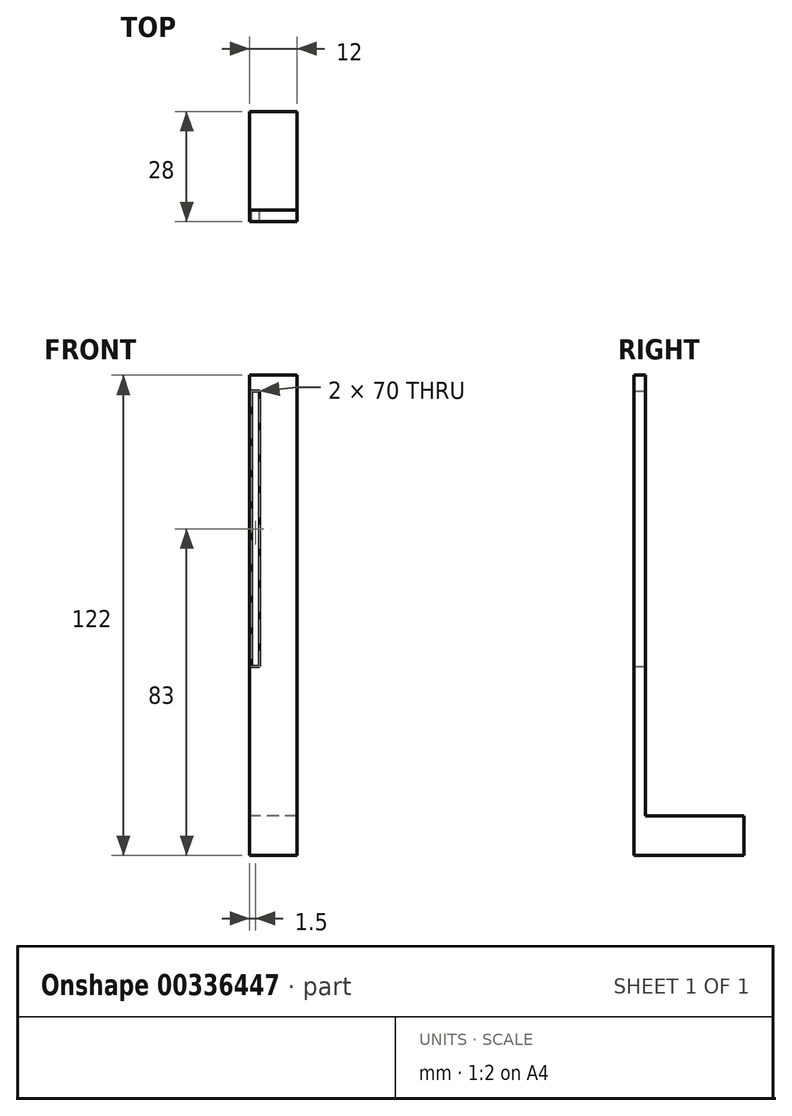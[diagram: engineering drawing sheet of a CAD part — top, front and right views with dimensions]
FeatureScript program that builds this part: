
annotation { "Feature Type Name" : "Feature", "Feature Type Description" : "" }
export const myFeature = defineFeature(function(context is Context, id is Id, definition is map)
    precondition{}
    {
        {
            var Q0;
            Q0=qCreatedBy(makeId("Right.planeOp"),FACE);
            var sketch = newSketch(context, id + "F0", { "sketchPlane" : qUnion([Q0])});
            skLineSegment(sketch, "E0.bottom", {"start": v(0, 0) * mm, "end": v(-3, 0) * mm});
            skLineSegment(sketch, "E0.top", {"start": v(0, 122) * mm, "end": v(-3, 122) * mm});
            skLineSegment(sketch, "E0.left", {"start": v(0, 0) * mm, "end": v(0, 122) * mm});
            skLineSegment(sketch, "E0.right", {"start": v(-3, 0) * mm, "end": v(-3, 122) * mm});
            skSolve(sketch);
        }
        {
            var Q0;
            Q0=qSketchRegion(id+"F0",true);
            extrude(context, id + "F1", {"entities" : qUnion([Q0]), "depth" : 12 * mm});
        }
        {
            var Q0;
            Q0=makeQuery(id+"F1.opExtrude","SWEPT_FACE",FACE,{"disambiguationData":[OSD([sQuery(id+"F0.wireOp",EDGE,"E0.left")])]});
            var sketch = newSketch(context, id + "F2", { "sketchPlane" : qUnion([Q0])});
            skLineSegment(sketch, "E1.bottom", {"start": v(-12, 0) * mm, "end": v(0, 0) * mm});
            skLineSegment(sketch, "E1.top", {"start": v(-12, 10) * mm, "end": v(0, 10) * mm});
            skLineSegment(sketch, "E1.left", {"start": v(-12, 0) * mm, "end": v(-12, 10) * mm});
            skLineSegment(sketch, "E1.right", {"start": v(0, 0) * mm, "end": v(0, 10) * mm});
            skSolve(sketch);
        }
        {
            var Q0;
            Q0=qSketchRegion(id+"F2",true);
            extrude(context, id + "F3", {"entities" : qUnion([Q0]), "operationType" : NewBodyOperationType.ADD, "depth" : 25 * mm});
        }
        {
            var Q0;
            Q0=makeQuery(id+"F1.opExtrude","SWEPT_FACE",FACE,{"disambiguationData":[OSD([sQuery(id+"F0.wireOp",EDGE,"E0.left")])]});
            var sketch = newSketch(context, id + "F4", { "sketchPlane" : qUnion([Q0])});
            skPoint(sketch, "E2.centerSnap0", {"position": v(-1.5, 122) * mm});
            skLineSegment(sketch, "E3", {"start": v(-1.5, 118) * mm, "end": v(-1.5, 48) * mm, "construction": true});
            skLineSegment(sketch, "E4", {"start": v(-1.5, 118) * mm, "end": v(-0.5, 118) * mm});
            skLineSegment(sketch, "E5", {"start": v(-0.5, 118) * mm, "end": v(-0.5, 48) * mm});
            skLineSegment(sketch, "E6", {"start": v(-0.5, 48) * mm, "end": v(-1.5, 48) * mm});
            skLineSegment(sketch, "E7.MirrorCS", {"start": v(-2.5, 118) * mm, "end": v(-2.5, 48) * mm});
            skLineSegment(sketch, "E8.MirrorCS", {"start": v(-1.5, 118) * mm, "end": v(-2.5, 118) * mm});
            skLineSegment(sketch, "E9.MirrorCS", {"start": v(-2.5, 48) * mm, "end": v(-1.5, 48) * mm});
            skSolve(sketch);
        }
        {
            var Q0;
            Q0=qSketchRegion(id+"F4",true);
            extrude(context, id + "F5", {"entities" : qUnion([Q0]), "operationType" : NewBodyOperationType.REMOVE, "endBound" : BoundingType.THROUGH_ALL, "oppositeDirection" : true, "depth" : 25 * mm});
        }
    });
